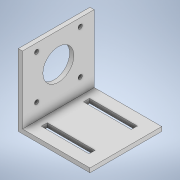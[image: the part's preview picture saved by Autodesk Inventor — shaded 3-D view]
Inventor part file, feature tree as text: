
AUTODESK INVENTOR PART (.ipt)
format: ipt  version: 2022 (Build 260153000, 153)  size: 143,360 bytes
history: native  units: mm
features: extrude x3, sketch x3
ambient origin geometry x8: Origin, YZ Plane, XZ Plane, XY Plane, X Axis, Y Axis, Z Axis, Center Point
bodies: Solid1 (feature_tree)
feature tree (6):
  extrude  "Extrusion1"  Depth=3.0mm
  extrude  "Extrusion2"  Depth=48.0mm
  extrude  "Extrusion3"  Depth=4.3mm
  sketch  "Sketch1"  dims[d0=51.0mm d1=3.0mm]
  sketch  "Sketch2"  dims[d2=48.0mm d3=48.0mm]
  sketch  "Sketch3"  dims[d4=51.0mm d5=0.0mm d7=22.0mm d12=3.0mm d13=3.0mm d14=51.0mm d15=0.0mm d16=12.865mm d17=2.15mm d18=9.0mm d20=7.85mm d21=270.0deg d22=2.15mm d23=4.3mm d24=0.0mm d25=0.0mm]
